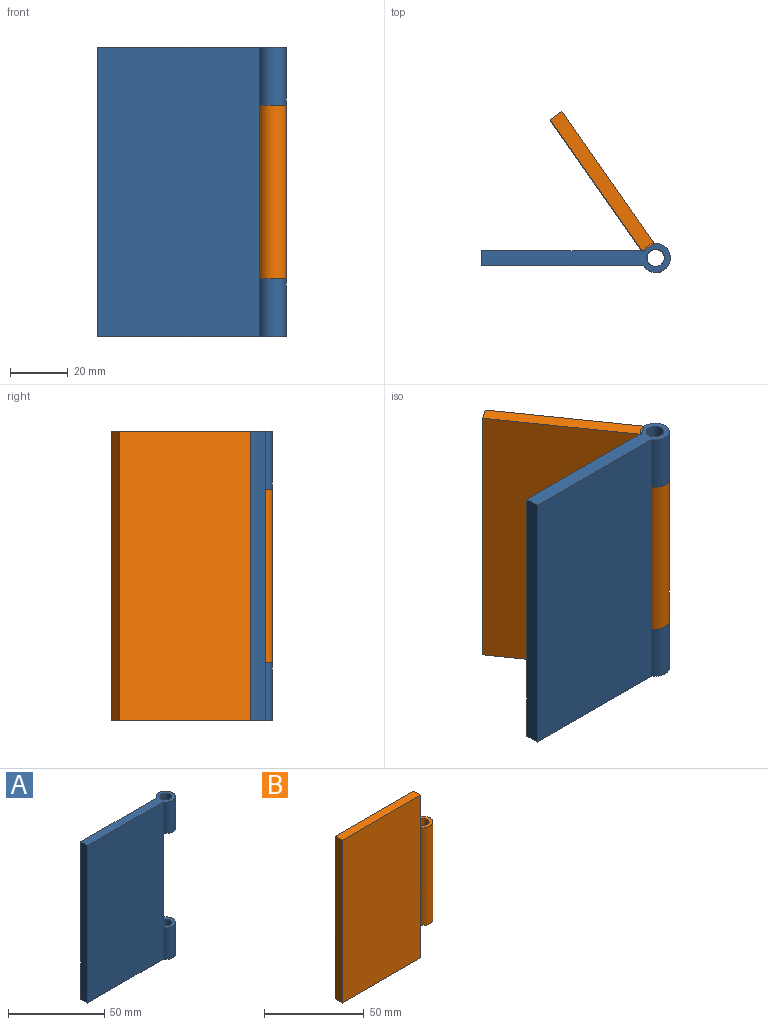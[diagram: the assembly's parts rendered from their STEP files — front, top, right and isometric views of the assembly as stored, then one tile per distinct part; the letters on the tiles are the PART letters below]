
ASSEMBLY  parts=2 mates=1
PART A: 12 faces, bbox 65x10x100 mm
  f0: cylinder r=5mm len=20mm, axis (0,0,1), area 523.6mm2, adj f2,f5,f6,f10
  f1: cylinder r=3mm len=20mm, axis (0,0,1), area 377mm2, adj f2,f10
  f2: plane 65x10mm, normal (0,0,1), area 326.4mm2, adj f0,f1,f3,f5,f6
  f3: plane 100x5mm, normal (-1,0,0), area 500mm2, adj f2,f4,f5,f6
  f4: plane 65x10mm, normal (0,0,-1), area 326.4mm2, adj f3,f5,f6,f7,f8
  f5: plane 100x55.67mm, normal (0,-1,0), area 5567mm2, adj f0,f2,f3,f4,f7,f11
  f6: plane 100x55.67mm, normal (0,1,0), area 5567mm2, adj f0,f2,f3,f4,f7,f11
  f7: cylinder r=5mm len=20mm, axis (0,0,1), area 523.6mm2, adj f4,f5,f6,f9
  f8: cylinder r=3mm len=20mm, axis (0,0,1), area 377mm2, adj f4,f9
  f9: plane 10x9.33mm, normal (0,0,1), area 48mm2, adj f7,f8,f11
  f10: plane 10x9.33mm, normal (0,0,-1), area 48mm2, adj f0,f1,f11
  f11: plane 60x5mm, normal (1,0,0), area 300mm2, adj f5,f6,f9,f10
PART B: 11 faces, bbox 65x10x100 mm
  f0: plane 55.67x5mm, normal (0,0,1), area 278.3mm2, adj f3,f4,f5,f7
  f1: plane 55.67x5mm, normal (0,0,-1), area 278.3mm2, adj f3,f4,f5,f9
  f2: cylinder r=5mm len=60mm, axis (0,0,1), area 1570.8mm2, adj f4,f5,f6,f8
  f3: plane 100x5mm, normal (-1,0,0), area 500mm2, adj f0,f1,f4,f5
  f4: plane 100x55.67mm, normal (0,-1,0), area 5567mm2, adj f0,f1,f2,f3,f7,f9
  f5: plane 100x55.67mm, normal (0,1,0), area 5567mm2, adj f0,f1,f2,f3,f7,f9
  f6: plane 10x9.33mm, normal (0,0,1), area 48mm2, adj f2,f7,f10
  f7: plane 20x5mm, normal (1,0,0), area 100mm2, adj f0,f4,f5,f6
  f8: plane 10x9.33mm, normal (0,0,-1), area 48mm2, adj f2,f9,f10
  f9: plane 20x5mm, normal (1,0,0), area 100mm2, adj f1,f4,f5,f8
  f10: cylinder r=3mm len=60mm, axis (0,0,1), area 1131mm2, adj f6,f8
PLACE A at identity fixed
PLACE B rot(axis=(0,0,-1),55deg) t=(-2.88,-10.52,0)mm
MATE cylindrical B.f2 <-> A.f0  axis (0,0,1) through (-11.55,-2.5,39.47)mm
